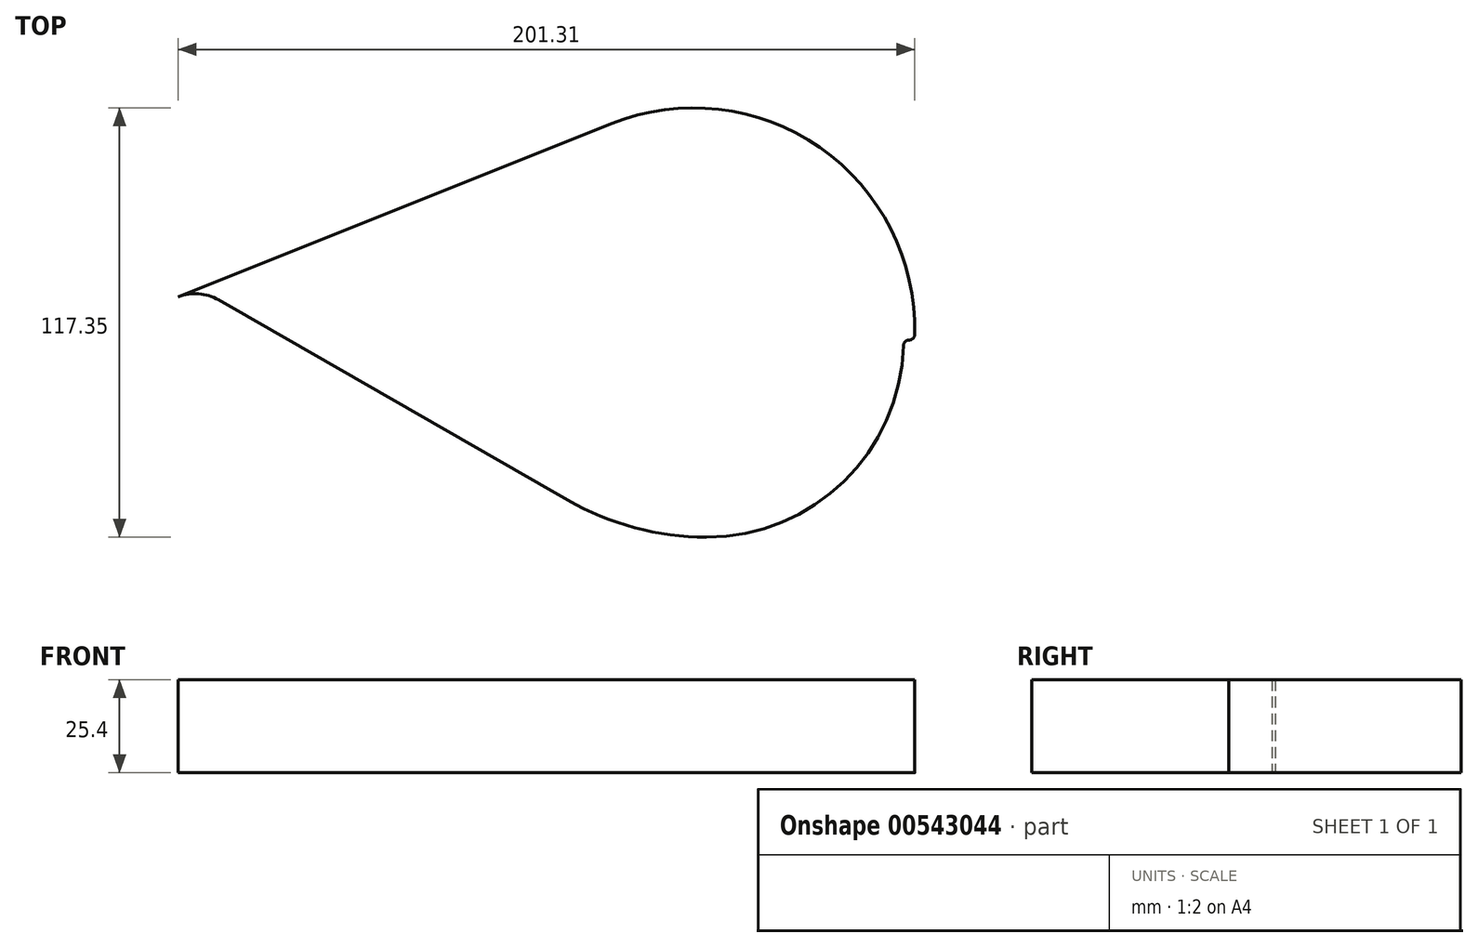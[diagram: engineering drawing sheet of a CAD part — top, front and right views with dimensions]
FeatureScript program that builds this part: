
annotation { "Feature Type Name" : "Feature", "Feature Type Description" : "" }
export const myFeature = defineFeature(function(context is Context, id is Id, definition is map)
    precondition{}
    {
        {
            var Q0;
            Q0=qCreatedBy(makeId("Top.planeOp"),FACE);
            var sketch = newSketch(context, id + "F0", { "sketchPlane" : qUnion([Q0])});
            skCircle(sketch, "E0", {"center": v(0, 0) * mm, "radius": 12.7 * mm});
            skLineSegment(sketch, "E1", {"start": v(0, 0) * mm, "end": v(139.7, 0) * mm, "construction": true});
            skLineSegment(sketch, "E2", {"start": v(139.7, 0) * mm, "end": v(195.05, 0) * mm, "construction": true});
            skArc(sketch, "E3", {"start": v(193.53, 1.48) * mm, "mid": v(177.25, 38.6) * mm, "end": v(139.7, 53.85) * mm});
            skArc(sketch, "E4", {"start": v(193.53, 1.48) * mm, "mid": v(195.05, 0) * mm, "end": v(196.57, 1.48) * mm});
            skLineSegment(sketch, "E5", {"start": v(195.05, 1.52) * mm, "end": v(195.05, 0) * mm, "construction": true});
            skArc(sketch, "E6", {"start": v(196.57, 1.48) * mm, "mid": v(170.68, 52.67) * mm, "end": v(113.68, 59.17) * mm});
            skLineSegment(sketch, "E7", {"start": v(-4.72, 11.8) * mm, "end": v(113.68, 59.17) * mm});
            skLineSegment(sketch, "E8", {"start": v(6.32, -11.02) * mm, "end": v(101.78, 43.75) * mm});
            skArc(sketch, "E9", {"start": v(139.7, 53.85) * mm, "mid": v(120.08, 51.28) * mm, "end": v(101.78, 43.75) * mm});
            skArc(sketch, "E10.MirrorCS", {"start": v(139.7, -53.85) * mm, "mid": v(120.08, -51.28) * mm, "end": v(101.78, -43.75) * mm});
            skLineSegment(sketch, "E11.MirrorCS", {"start": v(6.32, 11.02) * mm, "end": v(101.78, -43.75) * mm});
            skArc(sketch, "E12.MirrorCS", {"start": v(193.53, -1.48) * mm, "mid": v(177.25, -38.6) * mm, "end": v(139.7, -53.85) * mm});
            skArc(sketch, "E13.MirrorCS", {"start": v(193.53, -1.48) * mm, "mid": v(195.05, 0) * mm, "end": v(196.57, -1.48) * mm});
            skArc(sketch, "E14.MirrorCS", {"start": v(196.57, -1.48) * mm, "mid": v(170.68, -52.67) * mm, "end": v(113.68, -59.17) * mm});
            skLineSegment(sketch, "E15.MirrorCS", {"start": v(-4.72, -11.8) * mm, "end": v(113.68, -59.17) * mm});
            skLineSegment(sketch, "E16", {"start": v(139.7, 0) * mm, "end": v(139.7, 53.85) * mm, "construction": true});
            skLineSegment(sketch, "E17", {"start": v(113.68, 59.17) * mm, "end": v(139.7, -53.85) * mm, "construction": true});
            skSolve(sketch);
        }
        {
            var Q0;
            {var subQ3=sQuery(id+"F0.wireOp",EDGE,"E3");Q0=makeQuery(id+"F0.imprint","IMPRINT",FACE,{"disambiguationData":[TD([[makeQuery(id+"F0.imprint","IMPRINT",EDGE,{"derivedFrom":subQ3}),-1.0]])]});}
            var Q1;
            {var subQ1=sQuery(id+"F0.wireOp",EDGE,"E10.MirrorCS");Q1=makeQuery(id+"F0.imprint","IMPRINT",FACE,{"disambiguationData":[TD([[makeQuery(id+"F0.imprint","IMPRINT",EDGE,{"derivedFrom":subQ1}),1.0]])]});}
            extrude(context, id + "F1", {"entities" : qUnion([Q0, Q1]), "depth" : 25.4 * mm, "offsetDistance" : 25.4 * mm});
        }
    });
